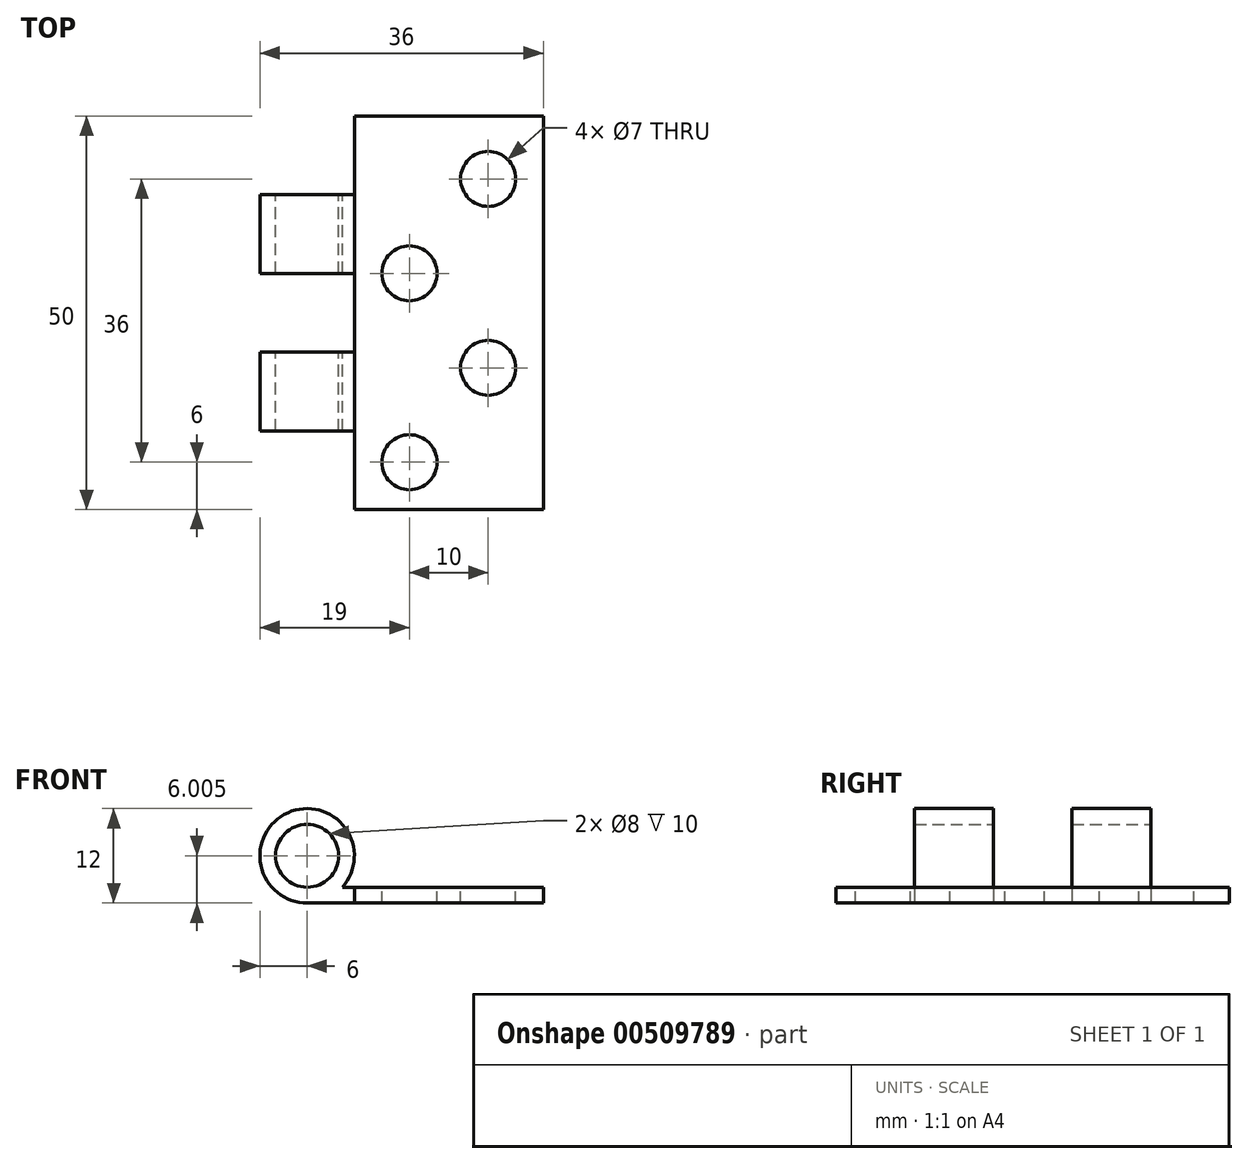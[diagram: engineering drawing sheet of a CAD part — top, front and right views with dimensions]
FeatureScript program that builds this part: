
annotation { "Feature Type Name" : "Feature", "Feature Type Description" : "" }
export const myFeature = defineFeature(function(context is Context, id is Id, definition is map)
    precondition{}
    {
        {
            var Q0;
            Q0=qCreatedBy(makeId("Front.planeOp"),FACE);
            var sketch = newSketch(context, id + "F0", { "sketchPlane" : qUnion([Q0])});
            skLineSegment(sketch, "E0", {"start": v(0.66, 30.5) * mm, "end": v(26.2, 30.5) * mm});
            skLineSegment(sketch, "E1", {"start": v(26.2, 30.5) * mm, "end": v(26.2, 28.5) * mm});
            skLineSegment(sketch, "E2", {"start": v(26.2, 28.5) * mm, "end": v(-3.8, 28.5) * mm});
            skArc(sketch, "E3", {"start": v(0.66, 30.5) * mm, "mid": v(-6.26, 39.98) * mm, "end": v(-3.8, 28.5) * mm});
            skCircle(sketch, "E4", {"center": v(-3.8, 34.5) * mm, "radius": 4 * mm});
            skSolve(sketch);
        }
        {
            var Q0;
            Q0=qSketchRegion(id+"F0",true);
            extrude(context, id + "F1", {"entities" : qUnion([Q0]), "depth" : 50 * mm});
        }
        {
            var Q0;
            Q0=makeQuery(id+"F1.opExtrude","SWEPT_FACE",FACE,{"disambiguationData":[OSD([sQuery(id+"F0.wireOp",EDGE,"E0")])]});
            var sketch = newSketch(context, id + "F2", { "sketchPlane" : qUnion([Q0])});
            skCircle(sketch, "E5", {"center": v(19.2, -8) * mm, "radius": 3.5 * mm});
            skCircle(sketch, "E6", {"center": v(19.2, -32) * mm, "radius": 3.5 * mm});
            skCircle(sketch, "E7", {"center": v(9.2, -20) * mm, "radius": 3.5 * mm});
            skCircle(sketch, "E8", {"center": v(9.2, -44) * mm, "radius": 3.5 * mm});
            skSolve(sketch);
        }
        {
            var Q0;
            Q0=makeQuery(id+"F2.imprint","IMPRINT",FACE,{"disambiguationData":[TD([[makeQuery(id+"F2.imprint","IMPRINT",EDGE,{"derivedFrom":sQuery(id+"F2.wireOp",EDGE,"E6")}),1.0]])]});
            var Q1;
            Q1=makeQuery(id+"F2.imprint","IMPRINT",FACE,{"disambiguationData":[TD([[makeQuery(id+"F2.imprint","IMPRINT",EDGE,{"derivedFrom":sQuery(id+"F2.wireOp",EDGE,"E8")}),1.0]])]});
            var Q2;
            Q2=makeQuery(id+"F2.imprint","IMPRINT",FACE,{"disambiguationData":[TD([[makeQuery(id+"F2.imprint","IMPRINT",EDGE,{"derivedFrom":sQuery(id+"F2.wireOp",EDGE,"E7")}),1.0]])]});
            var Q3;
            Q3=makeQuery(id+"F2.imprint","IMPRINT",FACE,{"disambiguationData":[TD([[makeQuery(id+"F2.imprint","IMPRINT",EDGE,{"derivedFrom":sQuery(id+"F2.wireOp",EDGE,"E5")}),1.0]])]});
            extrude(context, id + "F3", {"entities" : qUnion([Q0, Q1, Q2, Q3]), "operationType" : NewBodyOperationType.REMOVE, "endBound" : BoundingType.THROUGH_ALL, "oppositeDirection" : true, "depth" : 25 * mm});
        }
        {
            var Q0;
            Q0=makeQuery(id+"F1.opExtrude","SWEPT_FACE",FACE,{"disambiguationData":[OSD([sQuery(id+"F0.wireOp",EDGE,"E2")])]});
            var sketch = newSketch(context, id + "F4", { "sketchPlane" : qUnion([Q0])});
            skLineSegment(sketch, "E9.bottom", {"start": v(2.2, 50) * mm, "end": v(-12.05, 50) * mm});
            skLineSegment(sketch, "E9.top", {"start": v(2.2, 40) * mm, "end": v(-12.05, 40) * mm});
            skLineSegment(sketch, "E9.left", {"start": v(2.2, 50) * mm, "end": v(2.2, 40) * mm});
            skLineSegment(sketch, "E9.right", {"start": v(-12.05, 50) * mm, "end": v(-12.05, 40) * mm});
            skLineSegment(sketch, "E10.bottom", {"start": v(2.2, 30) * mm, "end": v(-12.73, 30) * mm});
            skLineSegment(sketch, "E10.top", {"start": v(2.2, 20) * mm, "end": v(-12.73, 20) * mm});
            skLineSegment(sketch, "E10.left", {"start": v(2.2, 30) * mm, "end": v(2.2, 20) * mm});
            skLineSegment(sketch, "E10.right", {"start": v(-12.73, 30) * mm, "end": v(-12.73, 20) * mm});
            skLineSegment(sketch, "E11.bottom", {"start": v(2.2, 10) * mm, "end": v(-13.48, 10) * mm});
            skLineSegment(sketch, "E11.top", {"start": v(2.2, 0) * mm, "end": v(-13.48, 0) * mm});
            skLineSegment(sketch, "E11.left", {"start": v(2.2, 10) * mm, "end": v(2.2, 0) * mm});
            skLineSegment(sketch, "E11.right", {"start": v(-13.48, 10) * mm, "end": v(-13.48, 0) * mm});
            skSolve(sketch);
        }
        {
            var Q0;
            Q0 = qSketchRegion(id + "F4", true);
            extrude(context, id + "F5", {"entities" : qUnion([Q0]), "operationType" : NewBodyOperationType.REMOVE, "oppositeDirection" : true, "depth" : 25 * mm});
        }
    });
